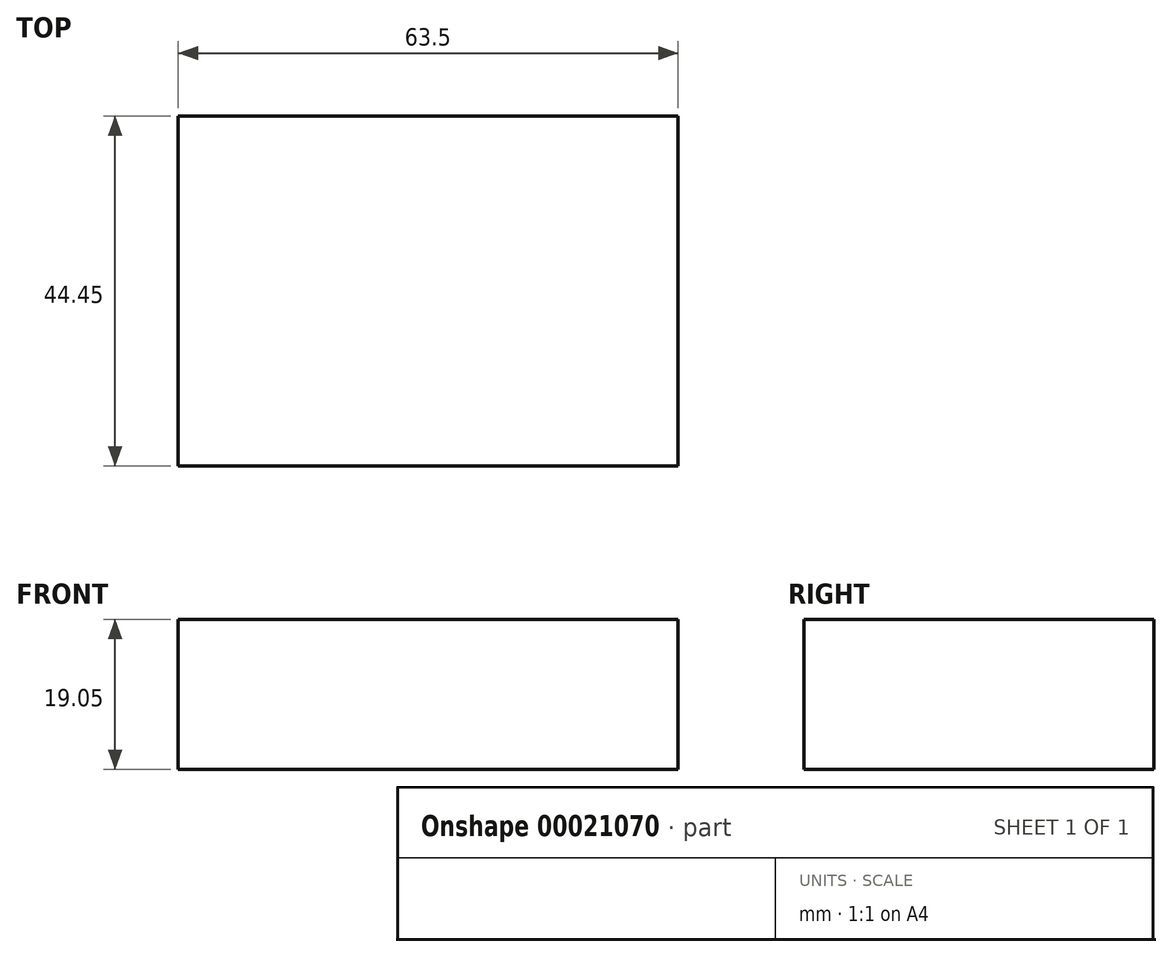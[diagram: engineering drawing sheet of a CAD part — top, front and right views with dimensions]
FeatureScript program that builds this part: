
annotation { "Feature Type Name" : "Feature", "Feature Type Description" : "" }
export const myFeature = defineFeature(function(context is Context, id is Id, definition is map)
    precondition{}
    {
        {
            var Q0;
            Q0=qCreatedBy(makeId("Front.planeOp"),FACE);
            var sketch = newSketch(context, id + "F0", { "sketchPlane" : qUnion([Q0])});
            skLineSegment(sketch, "E0.bottom", {"start": v(-30.38, 8.35) * mm, "end": v(33.12, 8.35) * mm});
            skLineSegment(sketch, "E0.top", {"start": v(-30.38, -10.7) * mm, "end": v(33.12, -10.7) * mm});
            skLineSegment(sketch, "E0.left", {"start": v(-30.38, 8.35) * mm, "end": v(-30.38, -10.7) * mm});
            skLineSegment(sketch, "E0.right", {"start": v(33.12, 8.35) * mm, "end": v(33.12, -10.7) * mm});
            skSolve(sketch);
        }
        {
            var Q0;
            Q0 = qSketchRegion(id + "F0", true);
            extrude(context, id + "F1", {"entities" : qUnion([Q0]), "depth" : 44.45 * mm});
        }
    });
